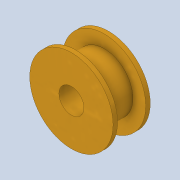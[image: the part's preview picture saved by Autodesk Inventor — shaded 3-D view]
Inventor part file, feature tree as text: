
AUTODESK INVENTOR PART (.ipt)
format: ipt  version: 2020.4 (Build 244396000, 396)  size: 122,368 bytes
history: native  units: mm
features: extrude x3, sketch x3, projected_geometry x1
ambient origin geometry x8: Origin, YZ Plane, XZ Plane, XY Plane, X Axis, Y Axis, Z Axis, Center Point
bodies: Solid1 (feature_tree)
feature tree (7):
  extrude  "Roller Base"  Depth=2.9mm TaperAngle=0.0deg
  extrude  "Roller Axis"  Depth=2.86mm TaperAngle=0.0deg
  extrude  "Roller Bar Fit"  Depth=2.2mm TaperAngle=0.0deg
  sketch  "Sketch1"  dims[d0=6.5mm d1=2.9mm d2=0.0mm]
  sketch  "Sketch2"  dims[d3=1.95mm d4=2.86mm d5=0.0mm]
  sketch  "Sketch3"  dims[d6=4.5mm d7=2.2mm d8=0.0mm]
  projected_geometry  "Projected Loop1"
